# Revit family: BIMLIB_Евроконус_для_медных_труб_ВР_РОСТерм
name_source: partatom
category: Соединительные детали трубопроводов
revit_build: Autodesk Revit 2017 (Build: 20170118_1100(x64)
units: mm (PartAtom-declared; Revit-internal decimal feet)

## family parameters
Всегда вертикально = Нет
На основе рабочей плоскости = Нет
Общий = Нет
При загрузке вырезать с полостями = Нет
Размер круглого соединителя = Использовать диаметр
Тип детали = Соединение

## types (1)
- Евроконус ВР для медных трубок
    ADSK_URL документации изделия = http://rostherm.ru
    ADSK_URL страницы изделия = http://rostherm.ru
    ADSK_Версия Revit = 2017
    ADSK_Единица измерения = шт.
    ADSK_Завод-изготовитель = РОСТерм
    ADSK_Код изделия = 500025
    ADSK_Марка = 500025
    ADSK_Масса = 0
    ADSK_Материал = BIMLIB_Медь_РТ
    ADSK_Наименование = Евроконус ВР 15х3/4
    ADSK_Наименование краткое = Евроконус ВР 15х3/4
    ADSK_Обозначение = ГОСТ 32415-2013
    BL_BIM library = https://bimlib.pro
    URL = http://rostherm.ru
    Изготовитель = РОСТерм
    Описание = Евроконус ВР для медных трубок
    РТ_D1 = 7.5 мм
    РТ_DN1 = 15 мм
    РТ_DN2 = 20 мм
    РТ_Dy = 5.75 мм
    РТ_Dy2 = 6 мм
    РТ_Dн = 8.1 мм
    РТ_H = 25.5 мм
    РТ_H1 = 20 мм

## geometry (parser evidence)
native form markers: Sweep x2
no freeform markers — native parametric forms only
